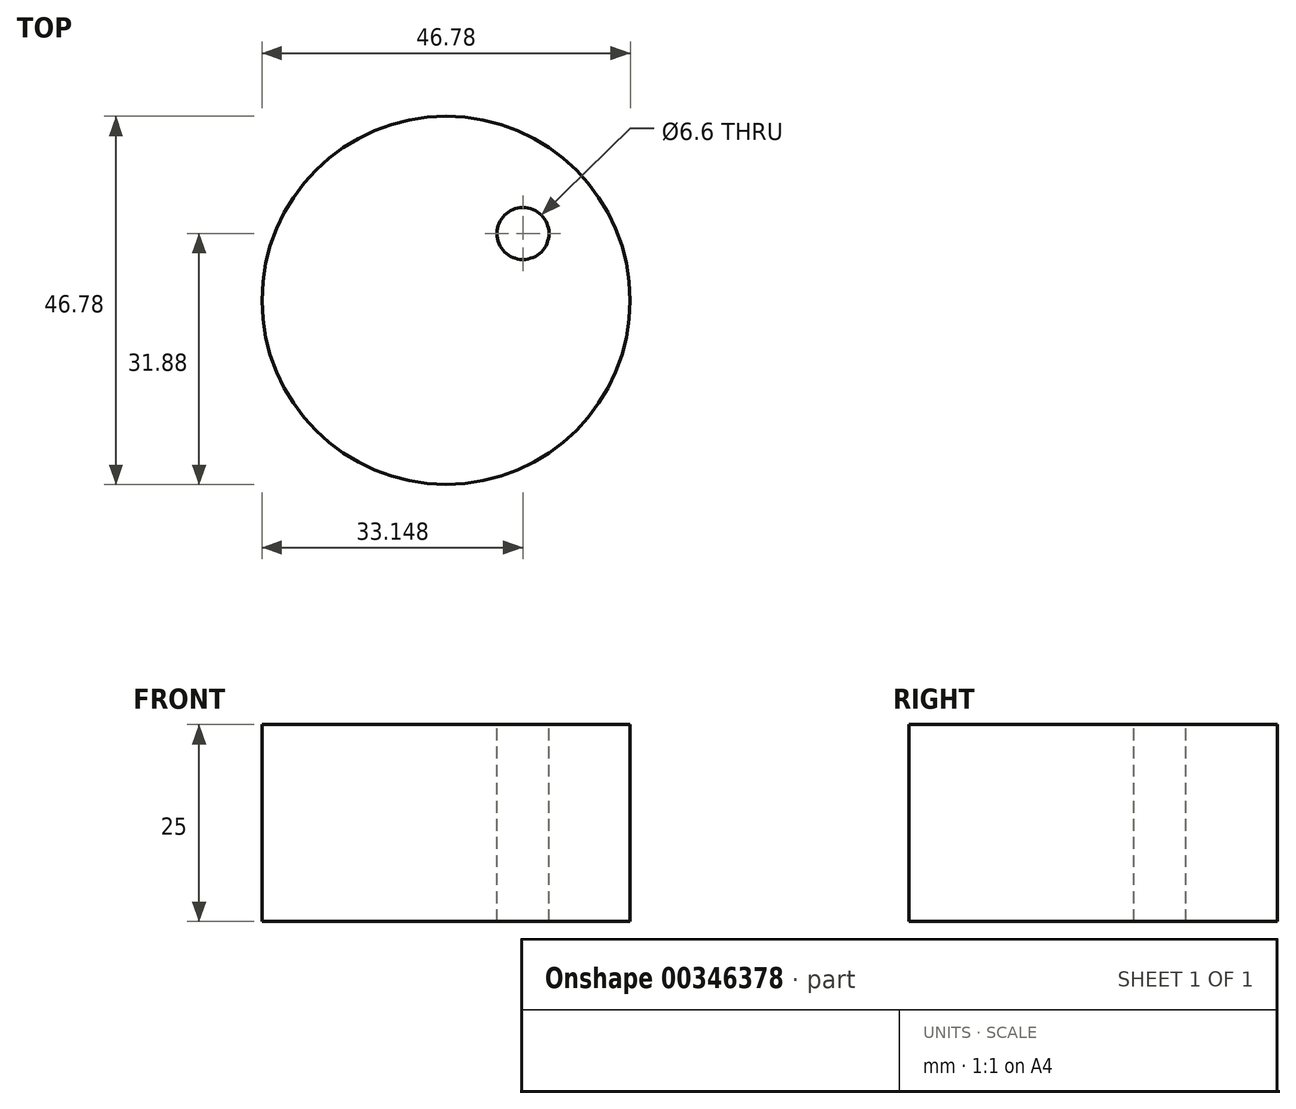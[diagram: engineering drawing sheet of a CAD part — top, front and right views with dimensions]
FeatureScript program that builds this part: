
annotation { "Feature Type Name" : "Feature", "Feature Type Description" : "" }
export const myFeature = defineFeature(function(context is Context, id is Id, definition is map)
    precondition{}
    {
        {
            var Q0;
            Q0=qCreatedBy(makeId("Top.planeOp"),FACE);
            var sketch = newSketch(context, id + "F0", { "sketchPlane" : qUnion([Q0])});
            skCircle(sketch, "E0", {"center": v(0, 0) * mm, "radius": 23.39 * mm});
            skSolve(sketch);
        }
        {
            var Q0;
            Q0 = qSketchRegion(id + "F0", true);
            extrude(context, id + "F1", {"entities" : qUnion([Q0]), "depth" : 25 * mm});
        }
        {
            var Q0;
            Q0=makeQuery(id+"F1.opExtrude","CAP_FACE",FACE,{"disambiguationData":[OSD([sQuery(id+"F0.wireOp",EDGE,"E0")])],"isStart":false});
            var sketch = newSketch(context, id + "F2", { "sketchPlane" : qUnion([Q0])});
            skPoint(sketch, "E1", {"position": v(9.76, 8.49) * mm});
            skSolve(sketch);
        }
        {
            var Q0;
            Q0=sQuery(id+"F2.wireOp",VERTEX,"E1");
            var Q1;
            Q1=makeQuery(id+"F1.opExtrude","SWEPT_BODY",BODY,{"disambiguationData":[OSD([sQuery(id+"F0.wireOp",EDGE,"E0")])]});
            hole(context, id + "F3", {"style" : HoleStyle.SIMPLE, "endStyle" : HoleEndStyle.THROUGH, "standardTappedOrClearance" : lookupTablePath({ "standard" : "ISO", "fit" : "Normal", "size" : "M6", "type" : "Clearance" }), "standardBlindInLast" : lookupTablePath({ "fit" : "Standard", "standard" : "ISO", "size" : "M6", "type" : "Clearance" }), "holeDiameter" : 6.6 * mm, "isTappedThrough" : true, "tappedDepth" : 12 * mm, "tapClearance" : 3, "locations" : qUnion([Q0]), "scope" : qUnion([Q1])});
        }
    });
